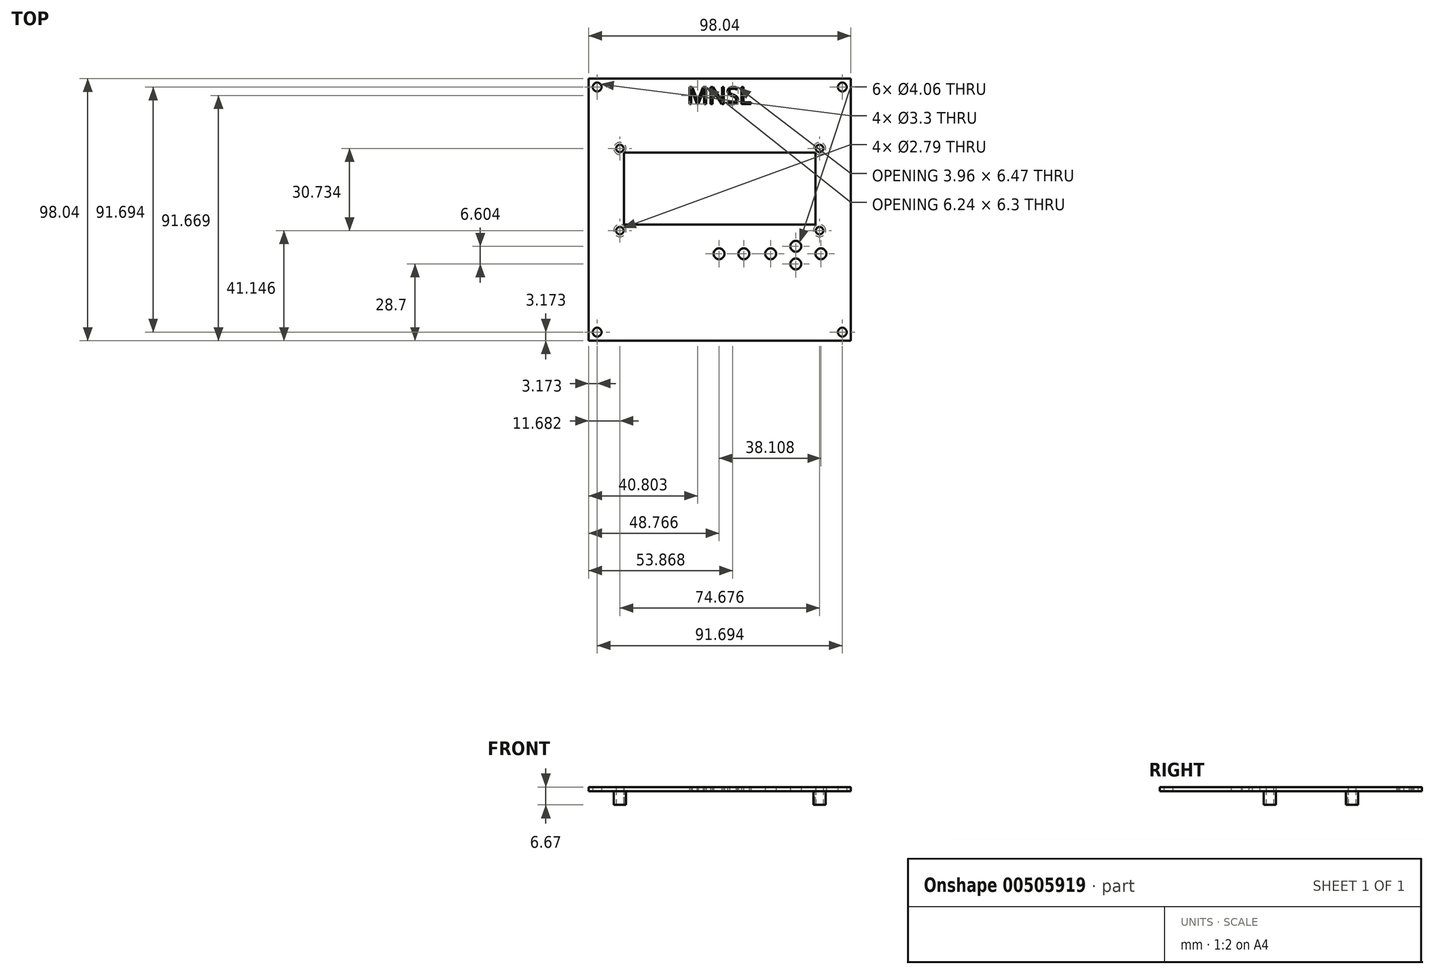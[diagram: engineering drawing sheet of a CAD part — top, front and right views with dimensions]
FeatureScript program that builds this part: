
annotation { "Feature Type Name" : "Feature", "Feature Type Description" : "" }
export const myFeature = defineFeature(function(context is Context, id is Id, definition is map)
    precondition{}
    {
        {
            var Q0;
            Q0=qCreatedBy(makeId("Top.planeOp"),FACE);
            var sketch = newSketch(context, id + "F0", { "sketchPlane" : qUnion([Q0])});
            skLineSegment(sketch, "E0.bottom", {"start": v(49.02, 49.02) * mm, "end": v(-49.02, 49.02) * mm});
            skLineSegment(sketch, "E0.top", {"start": v(49.02, -49.02) * mm, "end": v(-49.02, -49.02) * mm});
            skLineSegment(sketch, "E0.left", {"start": v(49.02, 49.02) * mm, "end": v(49.02, -49.02) * mm});
            skLineSegment(sketch, "E0.right", {"start": v(-49.02, 49.02) * mm, "end": v(-49.02, -49.02) * mm});
            skPoint(sketch, "E0.middle", {"position": v(0, 0) * mm});
            skLineSegment(sketch, "E1.bottom", {"start": v(49.02, 49.02) * mm, "end": v(42.67, 49.02) * mm, "construction": true});
            skLineSegment(sketch, "E1.top", {"start": v(49.02, 42.67) * mm, "end": v(42.67, 42.67) * mm, "construction": true});
            skLineSegment(sketch, "E1.left", {"start": v(49.02, 49.02) * mm, "end": v(49.02, 42.67) * mm, "construction": true});
            skLineSegment(sketch, "E1.right", {"start": v(42.67, 49.02) * mm, "end": v(42.67, 42.67) * mm, "construction": true});
            skLineSegment(sketch, "E2.bottom", {"start": v(-49.02, 49.02) * mm, "end": v(-42.67, 49.02) * mm, "construction": true});
            skLineSegment(sketch, "E2.top", {"start": v(-49.02, 42.67) * mm, "end": v(-42.67, 42.67) * mm, "construction": true});
            skLineSegment(sketch, "E2.left", {"start": v(-49.02, 49.02) * mm, "end": v(-49.02, 42.67) * mm, "construction": true});
            skLineSegment(sketch, "E2.right", {"start": v(-42.67, 49.02) * mm, "end": v(-42.67, 42.67) * mm, "construction": true});
            skLineSegment(sketch, "E3.bottom", {"start": v(-49.02, -49.02) * mm, "end": v(-42.67, -49.02) * mm, "construction": true});
            skLineSegment(sketch, "E3.top", {"start": v(-49.02, -42.67) * mm, "end": v(-42.67, -42.67) * mm, "construction": true});
            skLineSegment(sketch, "E3.left", {"start": v(-49.02, -49.02) * mm, "end": v(-49.02, -42.67) * mm, "construction": true});
            skLineSegment(sketch, "E3.right", {"start": v(-42.67, -49.02) * mm, "end": v(-42.67, -42.67) * mm, "construction": true});
            skLineSegment(sketch, "E4.bottom", {"start": v(49.02, -49.02) * mm, "end": v(42.67, -49.02) * mm, "construction": true});
            skLineSegment(sketch, "E4.top", {"start": v(49.02, -42.67) * mm, "end": v(42.67, -42.67) * mm, "construction": true});
            skLineSegment(sketch, "E4.left", {"start": v(49.02, -49.02) * mm, "end": v(49.02, -42.67) * mm, "construction": true});
            skLineSegment(sketch, "E4.right", {"start": v(42.67, -49.02) * mm, "end": v(42.67, -42.67) * mm, "construction": true});
            skLineSegment(sketch, "E5", {"start": v(-42.67, -42.67) * mm, "end": v(-49.02, -49.02) * mm, "construction": true});
            skLineSegment(sketch, "E6", {"start": v(-42.67, 42.67) * mm, "end": v(-49.02, 49.02) * mm, "construction": true});
            skLineSegment(sketch, "E7", {"start": v(49.02, 49.02) * mm, "end": v(42.67, 42.67) * mm, "construction": true});
            skLineSegment(sketch, "E8", {"start": v(49.02, -49.02) * mm, "end": v(42.67, -42.67) * mm, "construction": true});
            skCircle(sketch, "E9", {"center": v(45.85, -45.85) * mm, "radius": 1.65 * mm});
            skCircle(sketch, "E10", {"center": v(45.85, 45.85) * mm, "radius": 1.65 * mm});
            skCircle(sketch, "E11", {"center": v(-45.85, 45.85) * mm, "radius": 1.65 * mm});
            skCircle(sketch, "E12", {"center": v(-45.85, -45.85) * mm, "radius": 1.65 * mm});
            skLineSegment(sketch, "E13.bottom", {"start": v(39.88, 25.4) * mm, "end": v(-39.88, 25.4) * mm, "construction": true});
            skLineSegment(sketch, "E13.top", {"start": v(39.88, -25.4) * mm, "end": v(-39.88, -25.4) * mm, "construction": true});
            skLineSegment(sketch, "E13.left", {"start": v(39.88, 25.4) * mm, "end": v(39.88, -25.4) * mm, "construction": true});
            skLineSegment(sketch, "E13.right", {"start": v(-39.88, 25.4) * mm, "end": v(-39.88, -25.4) * mm, "construction": true});
            skLineSegment(sketch, "E14.bottom", {"start": v(-39.88, 25.4) * mm, "end": v(-37.34, 25.4) * mm, "construction": true});
            skLineSegment(sketch, "E14.top", {"start": v(-39.88, 22.86) * mm, "end": v(-37.34, 22.86) * mm, "construction": true});
            skLineSegment(sketch, "E14.left", {"start": v(-39.88, 25.4) * mm, "end": v(-39.88, 22.86) * mm, "construction": true});
            skLineSegment(sketch, "E14.right", {"start": v(-37.34, 25.4) * mm, "end": v(-37.34, 22.86) * mm, "construction": true});
            skCircle(sketch, "E15", {"center": v(-37.34, 22.86) * mm, "radius": 1.4 * mm});
            skLineSegment(sketch, "E16.bottom", {"start": v(-37.34, 22.86) * mm, "end": v(37.34, 22.86) * mm, "construction": true});
            skLineSegment(sketch, "E16.top", {"start": v(-37.34, -7.87) * mm, "end": v(37.34, -7.87) * mm, "construction": true});
            skLineSegment(sketch, "E16.left", {"start": v(-37.34, 22.86) * mm, "end": v(-37.34, -7.87) * mm, "construction": true});
            skLineSegment(sketch, "E16.right", {"start": v(37.34, 22.86) * mm, "end": v(37.34, -7.87) * mm, "construction": true});
            skCircle(sketch, "E17", {"center": v(37.34, 22.86) * mm, "radius": 1.4 * mm});
            skCircle(sketch, "E18", {"center": v(-37.34, -7.87) * mm, "radius": 1.4 * mm});
            skCircle(sketch, "E19", {"center": v(-37.34, 22.86) * mm, "radius": 2.29 * mm});
            skCircle(sketch, "E20", {"center": v(-37.34, -7.87) * mm, "radius": 2.29 * mm});
            skCircle(sketch, "E21", {"center": v(37.34, 22.86) * mm, "radius": 2.29 * mm});
            skLineSegment(sketch, "E22.bottom", {"start": v(-39.88, 25.4) * mm, "end": v(-35.81, 25.4) * mm, "construction": true});
            skLineSegment(sketch, "E22.top", {"start": v(-39.88, 21.34) * mm, "end": v(-35.81, 21.34) * mm, "construction": true});
            skLineSegment(sketch, "E22.left", {"start": v(-39.88, 25.4) * mm, "end": v(-39.88, 21.34) * mm, "construction": true});
            skLineSegment(sketch, "E22.right", {"start": v(-35.81, 25.4) * mm, "end": v(-35.81, 21.34) * mm, "construction": true});
            skLineSegment(sketch, "E23.bottom", {"start": v(-35.81, 21.34) * mm, "end": v(35.81, 21.34) * mm});
            skLineSegment(sketch, "E23.top", {"start": v(-35.81, -5.59) * mm, "end": v(35.81, -5.59) * mm});
            skLineSegment(sketch, "E23.left", {"start": v(-35.81, 21.34) * mm, "end": v(-35.81, -5.59) * mm});
            skLineSegment(sketch, "E23.right", {"start": v(35.81, 21.34) * mm, "end": v(35.81, -5.59) * mm});
            skLineSegment(sketch, "E24", {"start": v(-35.81, -5.59) * mm, "end": v(-5.33, -5.59) * mm, "construction": true});
            skLineSegment(sketch, "E25.bottom", {"start": v(-5.33, -10.16) * mm, "end": v(42.93, -10.16) * mm, "construction": true});
            skLineSegment(sketch, "E26", {"start": v(-45.85, 45.85) * mm, "end": v(45.85, 45.85) * mm, "construction": true});
            skLineSegment(sketch, "E27", {"start": v(-45.85, 45.85) * mm, "end": v(-45.85, -45.85) * mm, "construction": true});
            skCircle(sketch, "E28", {"center": v(37.34, -7.87) * mm, "radius": 1.4 * mm});
            skCircle(sketch, "E29", {"center": v(37.34, -7.87) * mm, "radius": 2.29 * mm});
            skLineSegment(sketch, "E30", {"start": v(-5.33, -5.59) * mm, "end": v(-5.33, -10.16) * mm, "construction": true});
            skText(sketch, "E31", { "text": "MNSL", "fontName": "OpenSans-Regular.ttf"});
            skLineSegment(sketch, "E32.top", {"start": v(-5.33, -16.51) * mm, "end": v(42.93, -16.51) * mm, "construction": true});
            skLineSegment(sketch, "E32.left", {"start": v(-5.33, -10.16) * mm, "end": v(-5.33, -16.51) * mm, "construction": true});
            skLineSegment(sketch, "E32.right", {"start": v(42.93, -10.16) * mm, "end": v(42.93, -16.51) * mm, "construction": true});
            skLineSegment(sketch, "E33", {"start": v(-5.33, -16.51) * mm, "end": v(-0.25, -16.51) * mm, "construction": true});
            skCircle(sketch, "E34", {"center": v(-0.25, -16.51) * mm, "radius": 2.03 * mm});
            skLineSegment(sketch, "E35", {"start": v(-5.33, -16.51) * mm, "end": v(9.02, -16.51) * mm, "construction": true});
            skLineSegment(sketch, "E36", {"start": v(-5.33, -16.51) * mm, "end": v(19.05, -16.51) * mm, "construction": true});
            skCircle(sketch, "E37", {"center": v(9.02, -16.51) * mm, "radius": 2.03 * mm});
            skCircle(sketch, "E38", {"center": v(19.05, -16.51) * mm, "radius": 2.03 * mm});
            skLineSegment(sketch, "E39", {"start": v(-5.33, -16.51) * mm, "end": v(37.85, -16.51) * mm, "construction": true});
            skCircle(sketch, "E40", {"center": v(37.85, -16.51) * mm, "radius": 2.03 * mm});
            skLineSegment(sketch, "E41.bottom", {"start": v(-5.33, -10.16) * mm, "end": v(28.45, -10.16) * mm, "construction": true});
            skLineSegment(sketch, "E41.top", {"start": v(-5.33, -20.32) * mm, "end": v(28.45, -20.32) * mm, "construction": true});
            skLineSegment(sketch, "E41.left", {"start": v(-5.33, -10.16) * mm, "end": v(-5.33, -20.32) * mm, "construction": true});
            skLineSegment(sketch, "E41.right", {"start": v(28.45, -10.16) * mm, "end": v(28.45, -20.32) * mm, "construction": true});
            skLineSegment(sketch, "E42", {"start": v(28.45, -10.16) * mm, "end": v(28.45, -13.72) * mm, "construction": true});
            skCircle(sketch, "E43", {"center": v(28.45, -13.72) * mm, "radius": 2.03 * mm});
            skCircle(sketch, "E44", {"center": v(28.45, -20.32) * mm, "radius": 2.03 * mm});
            const initialGuessF0  = {"E31": [-0.0122, 0.0395, 1, 0, 0.00635]};
            skSetInitialGuess(sketch, initialGuessF0);
            skSolve(sketch);
        }
        {
            var Q0;
            Q0=makeQuery(id+"F0.imprint","IMPRINT",FACE,{"disambiguationData":[TD([[makeQuery(id+"F0.imprint","IMPRINT",EDGE,{"derivedFrom":sQuery(id+"F0.wireOp",EDGE,"E17")}),-1.0]])]});
            var Q1;
            Q1=makeQuery(id+"F0.imprint","IMPRINT",FACE,{"disambiguationData":[TD([[makeQuery(id+"F0.imprint","IMPRINT",EDGE,{"derivedFrom":sQuery(id+"F0.wireOp",EDGE,"E15")}),-1.0]])]});
            var Q2;
            Q2=makeQuery(id+"F0.imprint","IMPRINT",FACE,{"disambiguationData":[TD([[makeQuery(id+"F0.imprint","IMPRINT",EDGE,{"derivedFrom":sQuery(id+"F0.wireOp",EDGE,"E18")}),-1.0]])]});
            var Q3;
            Q3=makeQuery(id+"F0.imprint","IMPRINT",FACE,{"disambiguationData":[TD([[makeQuery(id+"F0.imprint","IMPRINT",EDGE,{"derivedFrom":sQuery(id+"F0.wireOp",EDGE,"E28")}),-1.0]])]});
            var Q4;
            Q4=makeQuery(id+"F0.imprint","IMPRINT",FACE,{"disambiguationData":[TD([[makeQuery(id+"F0.imprint","IMPRINT",EDGE,{"derivedFrom":sQuery(id+"F0.wireOp",EDGE,"E0.bottom")}),1.0]])]});
            extrude(context, id + "F1", {"entities" : qUnion([Q0, Q1, Q2, Q3, Q4]), "depth" : 1.59 * mm, "offsetDistance" : 25.4 * mm});
        }
        {
            var Q0;
            Q0=makeQuery(id+"F0.imprint","IMPRINT",FACE,{"disambiguationData":[TD([[makeQuery(id+"F0.imprint","IMPRINT",EDGE,{"derivedFrom":sQuery(id+"F0.wireOp",EDGE,"E17")}),-1.0]])]});
            var Q1;
            Q1=makeQuery(id+"F0.imprint","IMPRINT",FACE,{"disambiguationData":[TD([[makeQuery(id+"F0.imprint","IMPRINT",EDGE,{"derivedFrom":sQuery(id+"F0.wireOp",EDGE,"E18")}),-1.0]])]});
            var Q2;
            Q2=makeQuery(id+"F0.imprint","IMPRINT",FACE,{"disambiguationData":[TD([[makeQuery(id+"F0.imprint","IMPRINT",EDGE,{"derivedFrom":sQuery(id+"F0.wireOp",EDGE,"E15")}),-1.0]])]});
            var Q3;
            Q3=makeQuery(id+"F0.imprint","IMPRINT",FACE,{"disambiguationData":[TD([[makeQuery(id+"F0.imprint","IMPRINT",EDGE,{"derivedFrom":sQuery(id+"F0.wireOp",EDGE,"E28")}),-1.0]])]});
            extrude(context, id + "F2", {"entities" : qUnion([Q0, Q1, Q2, Q3]), "operationType" : NewBodyOperationType.ADD, "oppositeDirection" : true, "depth" : 5.08 * mm});
        }
    });
